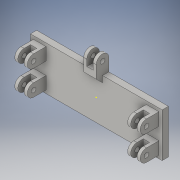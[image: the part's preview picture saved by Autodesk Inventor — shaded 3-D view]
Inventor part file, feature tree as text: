
AUTODESK INVENTOR PART (.ipt)
format: ipt  version: 2016 (Build 200138000, 138)  size: 237,056 bytes
history: native  units: in
note: dims shown in document units (in); Inventor stores cm internally (conversion verified against a paired STEP export)
features: sketch x8, extrude x7, fillet x2, chamfer x1
ambient origin geometry x8: Origin, YZ Plane, XZ Plane, XY Plane, X Axis, Y Axis, Z Axis, Center Point
bodies: Solid1 (feature_tree)
feature tree (18):
  extrude  "Extrusion1"  Depth=7.0in
  extrude  "Extrusion2"  Depth=20.0in
  extrude  "Extrusion3"  Depth=2.0in
  fillet  "Fillet1"  Radius=2.0in
  extrude  "Extrusion4"  Depth=2.0in
  sketch  "Sketch5"  dims[d10=2.0in d11=2.0in]
  extrude  "Extrusion5"  Depth=2.0in
  chamfer  "Chamfer1"  Distance=3.0in
  extrude  "Extrusion6"  Depth=1.0in
  fillet  "Fillet2"  Radius=0.75in
  extrude  "Extrusion7"  Depth=2.0in
  sketch  "Sketch1"  dims[d0=21.0in d1=7.0in]
  sketch  "Sketch2"  dims[d2=1.0in d3=0.0in d4=20.0in]
  sketch  "Sketch3"  dims[d5=6.0in d6=2.0in d7=2.0in]
  sketch  "Sketch4"  dims[d8=2.0in d9=2.0in]
  sketch  "Sketch6"  dims[d12=2.0in]
  sketch  "Sketch7"  dims[d13=2.0in d14=3.0in d15=0.0in]
  sketch  "Sketch8"  dims[d16=2.0in d17=0.0in d18=1.0in d19=0.75in d20=0.75in d21=22.0in d22=0.0in d23=2.0in d24=2.0in d25=3.0in d26=0.0in d27=1.0in d28=0.125in d29=45.0deg d30=2.0in d31=0.0in d32=1.0in d33=0.75in d34=2.0in d35=0.0in]
